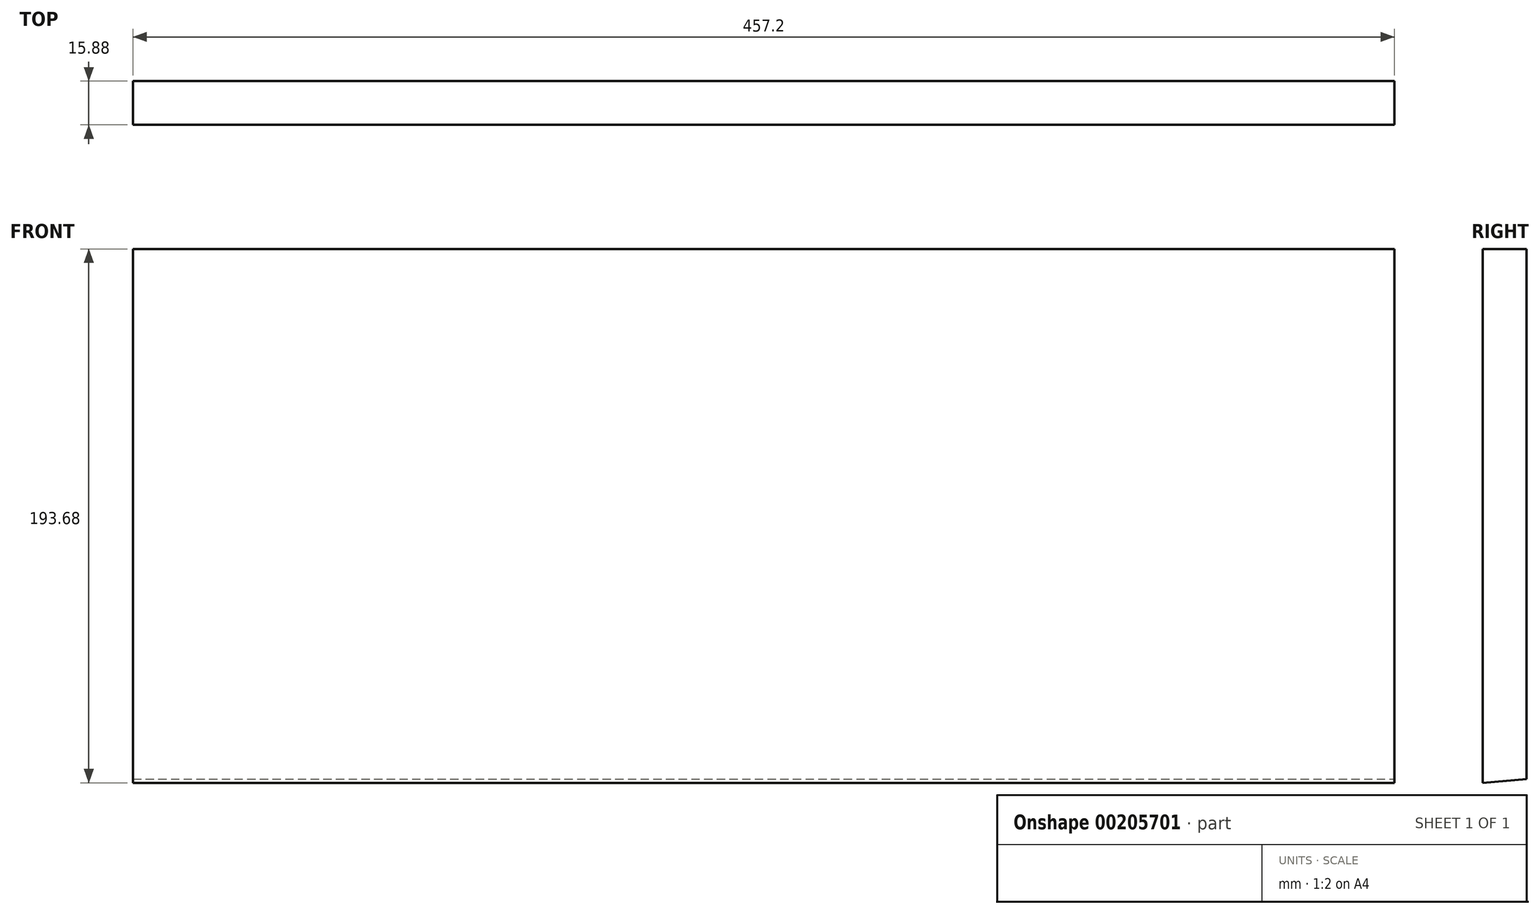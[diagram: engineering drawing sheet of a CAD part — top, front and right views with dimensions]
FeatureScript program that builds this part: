
annotation { "Feature Type Name" : "Feature", "Feature Type Description" : "" }
export const myFeature = defineFeature(function(context is Context, id is Id, definition is map)
    precondition{}
    {
        {
            var Q0;
            Q0=qCreatedBy(makeId("Front.planeOp"),FACE);
            var sketch = newSketch(context, id + "F0", { "sketchPlane" : qUnion([Q0])});
            skLineSegment(sketch, "E0.bottom", {"start": v(228.6, -96.84) * mm, "end": v(-228.6, -96.84) * mm});
            skLineSegment(sketch, "E0.top", {"start": v(228.6, 96.84) * mm, "end": v(-228.6, 96.84) * mm});
            skLineSegment(sketch, "E0.left", {"start": v(228.6, -96.84) * mm, "end": v(228.6, 96.84) * mm});
            skLineSegment(sketch, "E0.right", {"start": v(-228.6, -96.84) * mm, "end": v(-228.6, 96.84) * mm});
            skPoint(sketch, "E0.middle", {"position": v(0, 0) * mm});
            skSolve(sketch);
        }
        {
            var Q0;
            Q0=makeQuery(id+"F0.imprint","IMPRINT",FACE,{"disambiguationData":[TD([[makeQuery(id+"F0.imprint","IMPRINT",EDGE,{"derivedFrom":sQuery(id+"F0.wireOp",EDGE,"E0.bottom")}),-1.0]])]});
            extrude(context, id + "F1", {"entities" : qUnion([Q0]), "depth" : 15.88 * mm});
        }
        {
            var Q0;
            Q0=makeQuery(id+"F1.opExtrude","SWEPT_FACE",FACE,{"disambiguationData":[OSD([sQuery(id+"F0.wireOp",EDGE,"E0.left")])]});
            var sketch = newSketch(context, id + "F2", { "sketchPlane" : qUnion([Q0])});
            skLineSegment(sketch, "E1", {"start": v(-15.88, -96.84) * mm, "end": v(0, -95.45) * mm});
            skSolve(sketch);
        }
        {
            var Q0;
            {var subQ0=sQuery(id+"F2.wireOp",EDGE,"ee46kTFK-j3iO-CC9m-gRxn-7YBlTaNx6JAB");Q0=makeQuery(id+"F2.imprint","IMPRINT",FACE,{"disambiguationData":[TD([[makeQuery(id+"F2.imprint","IMPRINT",EDGE,{"derivedFrom":subQ0}),-1.0]])]});}
            var Q1;
            {var subQ0=sQuery(id+"F2.wireOp",EDGE,"E1");Q1=makeQuery(id+"F2.imprint","IMPRINT",FACE,{"disambiguationData":[TD([[makeQuery(id+"F2.imprint","IMPRINT",EDGE,{"derivedFrom":subQ0}),-1.0]])]});}
            extrude(context, id + "F3", {"entities" : qUnion([Q0, Q1]), "operationType" : NewBodyOperationType.REMOVE, "endBound" : BoundingType.THROUGH_ALL, "oppositeDirection" : true, "depth" : 25.4 * mm});
        }
    });
